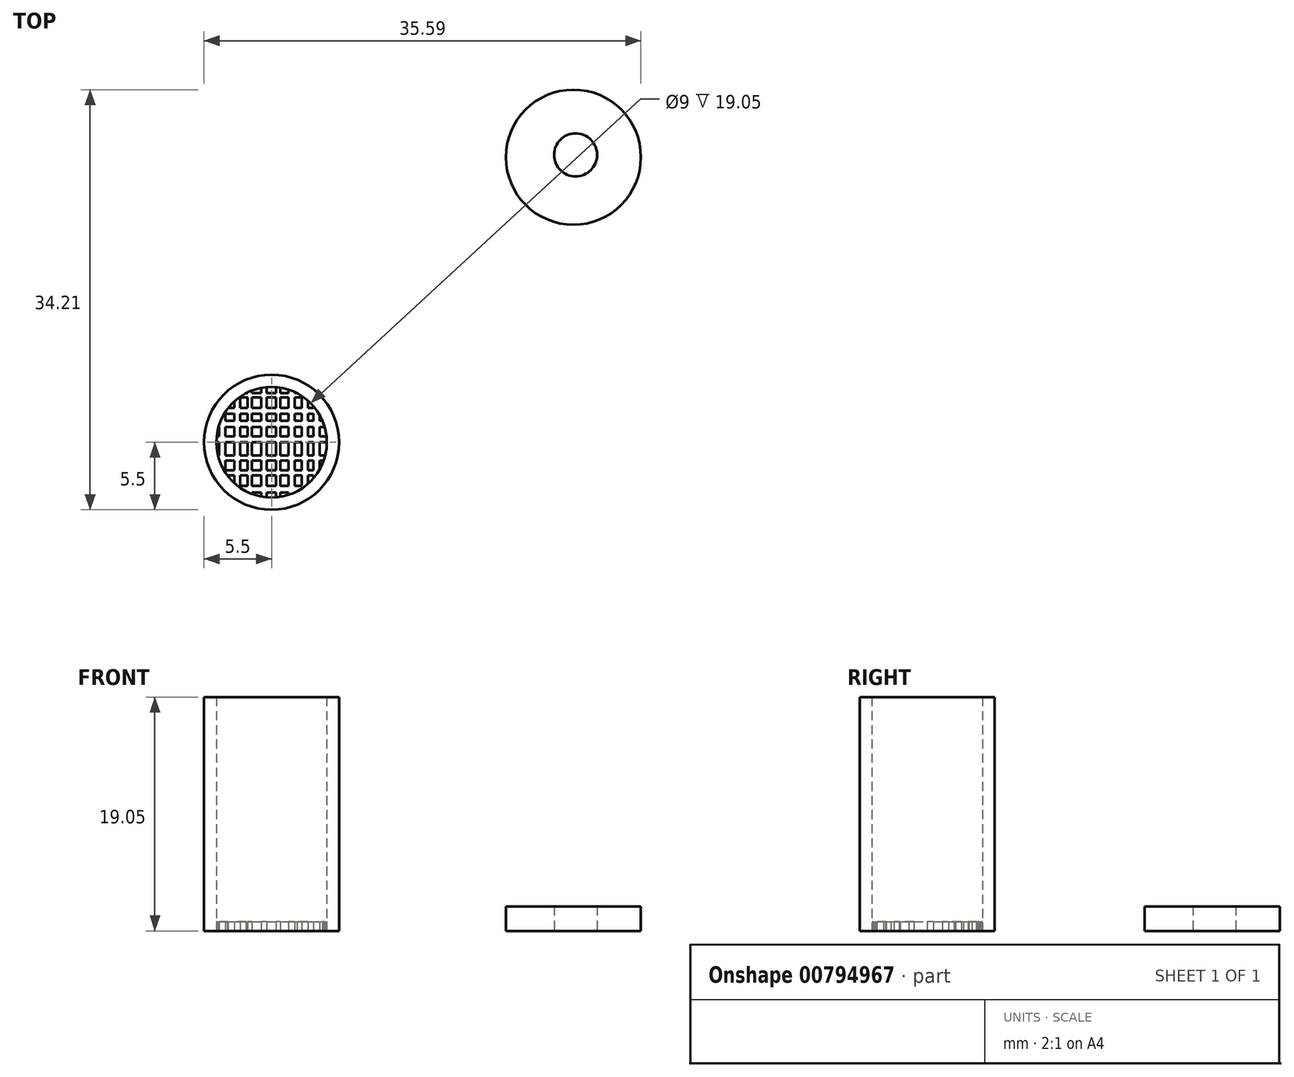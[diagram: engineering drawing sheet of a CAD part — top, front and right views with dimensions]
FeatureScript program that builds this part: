
annotation { "Feature Type Name" : "Feature", "Feature Type Description" : "" }
export const myFeature = defineFeature(function(context is Context, id is Id, definition is map)
    precondition{}
    {
        {
            var Q0;
            Q0=qCreatedBy(makeId("Top.planeOp"),FACE);
            var sketch = newSketch(context, id + "F0", { "sketchPlane" : qUnion([Q0])});
            skCircle(sketch, "E0", {"center": v(0, 0) * mm, "radius": 5.5 * mm});
            skSolve(sketch);
        }
        {
            var Q0;
            Q0=makeQuery(id+"F0.imprint","IMPRINT",FACE,{"disambiguationData":[TD([[makeQuery(id+"F0.imprint","IMPRINT",EDGE,{"derivedFrom":sQuery(id+"F0.wireOp",EDGE,"E0")}),1.0]])]});
            var Q1;
            Q1=sQuery(id+"F0.wireOp",EDGE,"E0");
            extrude(context, id + "F1", {"entities" : qUnion([Q0]), "surfaceEntities" : qUnion([Q1]), "depth" : 19.05 * mm, "offsetDistance" : 25.4 * mm});
        }
        {
            var Q0;
            Q0=qCreatedBy(makeId("Top.planeOp"),FACE);
            var sketch = newSketch(context, id + "F2", { "sketchPlane" : qUnion([Q0])});
            skCircle(sketch, "E1", {"center": v(0, 0) * mm, "radius": 4.5 * mm});
            skSolve(sketch);
        }
        {
            var Q0;
            Q0=makeQuery(id+"F2.imprint","IMPRINT",FACE,{"disambiguationData":[TD([[makeQuery(id+"F2.imprint","IMPRINT",EDGE,{"derivedFrom":sQuery(id+"F2.wireOp",EDGE,"E1")}),1.0]])]});
            extrude(context, id + "F3", {"entities" : qUnion([Q0]), "operationType" : NewBodyOperationType.REMOVE, "depth" : 76.7 * mm, "offsetDistance" : 25.4 * mm});
        }
        {
            var Q0;
            Q0=qCreatedBy(makeId("Top.planeOp"),FACE);
            var sketch = newSketch(context, id + "F4", { "sketchPlane" : qUnion([Q0])});
            skLineSegment(sketch, "E2.bottom", {"start": v(-4.27, -3.14) * mm, "end": v(-3.78, -3.14) * mm});
            skLineSegment(sketch, "E2.top", {"start": v(-4.27, 3.15) * mm, "end": v(-3.78, 3.15) * mm});
            skLineSegment(sketch, "E2.left", {"start": v(-4.27, -3.14) * mm, "end": v(-4.27, 3.15) * mm});
            skLineSegment(sketch, "E2.right", {"start": v(-3.78, -3.14) * mm, "end": v(-3.78, 3.15) * mm});
            skSolve(sketch);
        }
        {
            var Q0;
            Q0=makeQuery(id+"F4.imprint","IMPRINT",FACE,{"disambiguationData":[TD([[makeQuery(id+"F4.imprint","IMPRINT",EDGE,{"derivedFrom":sQuery(id+"F4.wireOp",EDGE,"E2.bottom")}),1.0]])]});
            extrude(context, id + "F5", {"entities" : qUnion([Q0]), "operationType" : NewBodyOperationType.ADD, "depth" : 0.76 * mm, "offsetDistance" : 25.4 * mm});
        }
        {
            var Q0;
            Q0=qCreatedBy(makeId("Top.planeOp"),FACE);
            var sketch = newSketch(context, id + "F6", { "sketchPlane" : qUnion([Q0])});
            skLineSegment(sketch, "E3.bottom", {"start": v(-3.03, -4) * mm, "end": v(-2.55, -4) * mm});
            skLineSegment(sketch, "E3.top", {"start": v(-3.03, 4.04) * mm, "end": v(-2.55, 4.04) * mm});
            skLineSegment(sketch, "E3.left", {"start": v(-3.03, -4) * mm, "end": v(-3.03, 4.04) * mm});
            skLineSegment(sketch, "E3.right", {"start": v(-2.55, -4) * mm, "end": v(-2.55, 4.04) * mm});
            skSolve(sketch);
        }
        {
            var Q0;
            Q0=makeQuery(id+"F6.imprint","IMPRINT",FACE,{"disambiguationData":[TD([[makeQuery(id+"F6.imprint","IMPRINT",EDGE,{"derivedFrom":sQuery(id+"F6.wireOp",EDGE,"E3.bottom")}),1.0]])]});
            extrude(context, id + "F7", {"entities" : qUnion([Q0]), "operationType" : NewBodyOperationType.ADD, "depth" : 0.76 * mm, "offsetDistance" : 25.4 * mm});
        }
        {
            var Q0;
            Q0=qCreatedBy(makeId("Top.planeOp"),FACE);
            var sketch = newSketch(context, id + "F8", { "sketchPlane" : qUnion([Q0])});
            skLineSegment(sketch, "E4.bottom", {"start": v(-1.96, -4.6) * mm, "end": v(-1.6, -4.6) * mm});
            skLineSegment(sketch, "E4.top", {"start": v(-1.96, 4.74) * mm, "end": v(-1.6, 4.74) * mm});
            skLineSegment(sketch, "E4.left", {"start": v(-1.96, -4.6) * mm, "end": v(-1.96, 4.74) * mm});
            skLineSegment(sketch, "E4.right", {"start": v(-1.6, -4.6) * mm, "end": v(-1.6, 4.74) * mm});
            skSolve(sketch);
        }
        {
            var Q0;
            Q0=makeQuery(id+"F8.imprint","IMPRINT",FACE,{"disambiguationData":[TD([[makeQuery(id+"F8.imprint","IMPRINT",EDGE,{"derivedFrom":sQuery(id+"F8.wireOp",EDGE,"E4.bottom")}),1.0]])]});
            extrude(context, id + "F9", {"entities" : qUnion([Q0]), "operationType" : NewBodyOperationType.ADD, "depth" : 0.76 * mm, "offsetDistance" : 25.4 * mm});
        }
        {
            var Q0;
            Q0=qCreatedBy(makeId("Top.planeOp"),FACE);
            var sketch = newSketch(context, id + "F10", { "sketchPlane" : qUnion([Q0])});
            skLineSegment(sketch, "E5.bottom", {"start": v(-0.85, -5.13) * mm, "end": v(-0.4, -5.13) * mm});
            skLineSegment(sketch, "E5.top", {"start": v(-0.85, 5) * mm, "end": v(-0.4, 5) * mm});
            skLineSegment(sketch, "E5.left", {"start": v(-0.85, -5.13) * mm, "end": v(-0.85, 5) * mm});
            skLineSegment(sketch, "E5.right", {"start": v(-0.4, -5.13) * mm, "end": v(-0.4, 5) * mm});
            skSolve(sketch);
        }
        {
            var Q0;
            Q0=makeQuery(id+"F10.imprint","IMPRINT",FACE,{"disambiguationData":[TD([[makeQuery(id+"F10.imprint","IMPRINT",EDGE,{"derivedFrom":sQuery(id+"F10.wireOp",EDGE,"E5.bottom")}),1.0]])]});
            extrude(context, id + "F11", {"entities" : qUnion([Q0]), "operationType" : NewBodyOperationType.ADD, "depth" : 0.76 * mm, "offsetDistance" : 25.4 * mm});
        }
        {
            var Q0;
            Q0=qCreatedBy(makeId("Top.planeOp"),FACE);
            var sketch = newSketch(context, id + "F12", { "sketchPlane" : qUnion([Q0])});
            skLineSegment(sketch, "E6.bottom", {"start": v(0.35, -5) * mm, "end": v(0.72, -5) * mm});
            skLineSegment(sketch, "E6.top", {"start": v(0.35, 4.95) * mm, "end": v(0.72, 4.95) * mm});
            skLineSegment(sketch, "E6.left", {"start": v(0.35, -5) * mm, "end": v(0.35, 4.95) * mm});
            skLineSegment(sketch, "E6.right", {"start": v(0.72, -5) * mm, "end": v(0.72, 4.95) * mm});
            skSolve(sketch);
        }
        {
            var Q0;
            Q0=makeQuery(id+"F12.imprint","IMPRINT",FACE,{"disambiguationData":[TD([[makeQuery(id+"F12.imprint","IMPRINT",EDGE,{"derivedFrom":sQuery(id+"F12.wireOp",EDGE,"E6.bottom")}),1.0]])]});
            extrude(context, id + "F13", {"entities" : qUnion([Q0]), "operationType" : NewBodyOperationType.ADD, "depth" : 0.76 * mm, "offsetDistance" : 25.4 * mm});
        }
        {
            var Q0;
            Q0=qCreatedBy(makeId("Top.planeOp"),FACE);
            var sketch = newSketch(context, id + "F14", { "sketchPlane" : qUnion([Q0])});
            skLineSegment(sketch, "E7.bottom", {"start": v(1.38, -4.88) * mm, "end": v(1.88, -4.88) * mm});
            skLineSegment(sketch, "E7.top", {"start": v(1.38, 4.62) * mm, "end": v(1.88, 4.62) * mm});
            skLineSegment(sketch, "E7.left", {"start": v(1.38, -4.88) * mm, "end": v(1.38, 4.62) * mm});
            skLineSegment(sketch, "E7.right", {"start": v(1.88, -4.88) * mm, "end": v(1.88, 4.62) * mm});
            skSolve(sketch);
        }
        {
            var Q0;
            Q0=makeQuery(id+"F14.imprint","IMPRINT",FACE,{"disambiguationData":[TD([[makeQuery(id+"F14.imprint","IMPRINT",EDGE,{"derivedFrom":sQuery(id+"F14.wireOp",EDGE,"E7.bottom")}),1.0]])]});
            extrude(context, id + "F15", {"entities" : qUnion([Q0]), "operationType" : NewBodyOperationType.ADD, "depth" : 0.76 * mm, "offsetDistance" : 25.4 * mm});
        }
        {
            var Q0;
            Q0=qCreatedBy(makeId("Top.planeOp"),FACE);
            var sketch = newSketch(context, id + "F16", { "sketchPlane" : qUnion([Q0])});
            skLineSegment(sketch, "E8.bottom", {"start": v(2.47, -4.47) * mm, "end": v(2.95, -4.47) * mm});
            skLineSegment(sketch, "E8.top", {"start": v(2.47, 4.18) * mm, "end": v(2.95, 4.18) * mm});
            skLineSegment(sketch, "E8.left", {"start": v(2.47, -4.47) * mm, "end": v(2.47, 4.18) * mm});
            skLineSegment(sketch, "E8.right", {"start": v(2.95, -4.47) * mm, "end": v(2.95, 4.18) * mm});
            skSolve(sketch);
        }
        {
            var Q0;
            Q0=makeQuery(id+"F16.imprint","IMPRINT",FACE,{"disambiguationData":[TD([[makeQuery(id+"F16.imprint","IMPRINT",EDGE,{"derivedFrom":sQuery(id+"F16.wireOp",EDGE,"E8.bottom")}),1.0]])]});
            extrude(context, id + "F17", {"entities" : qUnion([Q0]), "operationType" : NewBodyOperationType.ADD, "depth" : 0.76 * mm, "offsetDistance" : 25.4 * mm});
        }
        {
            var Q0;
            Q0=qCreatedBy(makeId("Top.planeOp"),FACE);
            var sketch = newSketch(context, id + "F18", { "sketchPlane" : qUnion([Q0])});
            skLineSegment(sketch, "E9.bottom", {"start": v(3.4, -3.7) * mm, "end": v(3.92, -3.7) * mm});
            skLineSegment(sketch, "E9.top", {"start": v(3.4, 3.35) * mm, "end": v(3.92, 3.35) * mm});
            skLineSegment(sketch, "E9.left", {"start": v(3.4, -3.7) * mm, "end": v(3.4, 3.35) * mm});
            skLineSegment(sketch, "E9.right", {"start": v(3.92, -3.7) * mm, "end": v(3.92, 3.35) * mm});
            skSolve(sketch);
        }
        {
            var Q0;
            Q0=makeQuery(id+"F18.imprint","IMPRINT",FACE,{"disambiguationData":[TD([[makeQuery(id+"F18.imprint","IMPRINT",EDGE,{"derivedFrom":sQuery(id+"F18.wireOp",EDGE,"E9.bottom")}),1.0]])]});
            extrude(context, id + "F19", {"entities" : qUnion([Q0]), "operationType" : NewBodyOperationType.ADD, "depth" : 0.76 * mm, "offsetDistance" : 25.4 * mm});
        }
        {
            var Q0;
            Q0=qCreatedBy(makeId("Top.planeOp"),FACE);
            var sketch = newSketch(context, id + "F20", { "sketchPlane" : qUnion([Q0])});
            skLineSegment(sketch, "E10.bottom", {"start": v(-3.42, -4.1) * mm, "end": v(3.33, -4.1) * mm});
            skLineSegment(sketch, "E10.top", {"start": v(-3.42, -3.57) * mm, "end": v(3.33, -3.57) * mm});
            skLineSegment(sketch, "E10.left", {"start": v(-3.42, -4.1) * mm, "end": v(-3.42, -3.57) * mm});
            skLineSegment(sketch, "E10.right", {"start": v(3.33, -4.1) * mm, "end": v(3.33, -3.57) * mm});
            skSolve(sketch);
        }
        {
            var Q0;
            Q0=makeQuery(id+"F20.imprint","IMPRINT",FACE,{"disambiguationData":[TD([[makeQuery(id+"F20.imprint","IMPRINT",EDGE,{"derivedFrom":sQuery(id+"F20.wireOp",EDGE,"E10.bottom")}),1.0]])]});
            extrude(context, id + "F21", {"entities" : qUnion([Q0]), "operationType" : NewBodyOperationType.ADD, "depth" : 0.76 * mm, "offsetDistance" : 25.4 * mm});
        }
        {
            var Q0;
            Q0=qCreatedBy(makeId("Top.planeOp"),FACE);
            var sketch = newSketch(context, id + "F22", { "sketchPlane" : qUnion([Q0])});
            skLineSegment(sketch, "E11.bottom", {"start": v(-4.08, -2.7) * mm, "end": v(4.2, -2.7) * mm});
            skLineSegment(sketch, "E11.top", {"start": v(-4.08, -2.3) * mm, "end": v(4.2, -2.3) * mm});
            skLineSegment(sketch, "E11.left", {"start": v(-4.08, -2.7) * mm, "end": v(-4.08, -2.3) * mm});
            skLineSegment(sketch, "E11.right", {"start": v(4.2, -2.7) * mm, "end": v(4.2, -2.3) * mm});
            skSolve(sketch);
        }
        {
            var Q0;
            Q0=makeQuery(id+"F22.imprint","IMPRINT",FACE,{"disambiguationData":[TD([[makeQuery(id+"F22.imprint","IMPRINT",EDGE,{"derivedFrom":sQuery(id+"F22.wireOp",EDGE,"E11.bottom")}),1.0]])]});
            extrude(context, id + "F23", {"entities" : qUnion([Q0]), "operationType" : NewBodyOperationType.ADD, "depth" : 0.76 * mm, "offsetDistance" : 25.4 * mm});
        }
        {
            var Q0;
            Q0=qCreatedBy(makeId("Top.planeOp"),FACE);
            var sketch = newSketch(context, id + "F24", { "sketchPlane" : qUnion([Q0])});
            skLineSegment(sketch, "E12.bottom", {"start": v(-4.87, -1.5) * mm, "end": v(5, -1.5) * mm});
            skLineSegment(sketch, "E12.top", {"start": v(-4.87, -1.07) * mm, "end": v(5, -1.07) * mm});
            skLineSegment(sketch, "E12.left", {"start": v(-4.87, -1.5) * mm, "end": v(-4.87, -1.07) * mm});
            skLineSegment(sketch, "E12.right", {"start": v(5, -1.5) * mm, "end": v(5, -1.07) * mm});
            skSolve(sketch);
        }
        {
            var Q0;
            Q0=makeQuery(id+"F24.imprint","IMPRINT",FACE,{"disambiguationData":[TD([[makeQuery(id+"F24.imprint","IMPRINT",EDGE,{"derivedFrom":sQuery(id+"F24.wireOp",EDGE,"E12.bottom")}),1.0]])]});
            extrude(context, id + "F25", {"entities" : qUnion([Q0]), "operationType" : NewBodyOperationType.ADD, "depth" : 0.76 * mm, "offsetDistance" : 25.4 * mm});
        }
        {
            var Q0;
            Q0=qCreatedBy(makeId("Top.planeOp"),FACE);
            var sketch = newSketch(context, id + "F26", { "sketchPlane" : qUnion([Q0])});
            skLineSegment(sketch, "E13.bottom", {"start": v(-4.98, 0) * mm, "end": v(4.97, 0) * mm});
            skLineSegment(sketch, "E13.top", {"start": v(-4.98, 0.49) * mm, "end": v(4.97, 0.49) * mm});
            skLineSegment(sketch, "E13.left", {"start": v(-4.98, 0) * mm, "end": v(-4.98, 0.49) * mm});
            skLineSegment(sketch, "E13.right", {"start": v(4.97, 0) * mm, "end": v(4.97, 0.49) * mm});
            skSolve(sketch);
        }
        {
            var Q0;
            Q0=makeQuery(id+"F26.imprint","IMPRINT",FACE,{"disambiguationData":[TD([[makeQuery(id+"F26.imprint","IMPRINT",EDGE,{"derivedFrom":sQuery(id+"F26.wireOp",EDGE,"E13.bottom")}),1.0]])]});
            extrude(context, id + "F27", {"entities" : qUnion([Q0]), "operationType" : NewBodyOperationType.ADD, "depth" : 0.76 * mm, "offsetDistance" : 25.4 * mm});
        }
        {
            var Q0;
            Q0=qCreatedBy(makeId("Top.planeOp"),FACE);
            var sketch = newSketch(context, id + "F28", { "sketchPlane" : qUnion([Q0])});
            skLineSegment(sketch, "E14.bottom", {"start": v(-4.72, 1.23) * mm, "end": v(4.8, 1.23) * mm});
            skLineSegment(sketch, "E14.top", {"start": v(-4.72, 1.74) * mm, "end": v(4.8, 1.74) * mm});
            skLineSegment(sketch, "E14.left", {"start": v(-4.72, 1.23) * mm, "end": v(-4.72, 1.74) * mm});
            skLineSegment(sketch, "E14.right", {"start": v(4.8, 1.23) * mm, "end": v(4.8, 1.74) * mm});
            skSolve(sketch);
        }
        {
            var Q0;
            Q0=makeQuery(id+"F28.imprint","IMPRINT",FACE,{"disambiguationData":[TD([[makeQuery(id+"F28.imprint","IMPRINT",EDGE,{"derivedFrom":sQuery(id+"F28.wireOp",EDGE,"E14.bottom")}),1.0]])]});
            extrude(context, id + "F29", {"entities" : qUnion([Q0]), "operationType" : NewBodyOperationType.ADD, "depth" : 0.76 * mm, "offsetDistance" : 25.4 * mm});
        }
        {
            var Q0;
            Q0=qCreatedBy(makeId("Top.planeOp"),FACE);
            var sketch = newSketch(context, id + "F30", { "sketchPlane" : qUnion([Q0])});
            skLineSegment(sketch, "E15.bottom", {"start": v(-4.41, 2.3) * mm, "end": v(4.45, 2.3) * mm});
            skLineSegment(sketch, "E15.top", {"start": v(-4.41, 2.78) * mm, "end": v(4.45, 2.78) * mm});
            skLineSegment(sketch, "E15.left", {"start": v(-4.41, 2.3) * mm, "end": v(-4.41, 2.78) * mm});
            skLineSegment(sketch, "E15.right", {"start": v(4.45, 2.3) * mm, "end": v(4.45, 2.78) * mm});
            skSolve(sketch);
        }
        {
            var Q0;
            Q0=makeQuery(id+"F30.imprint","IMPRINT",FACE,{"disambiguationData":[TD([[makeQuery(id+"F30.imprint","IMPRINT",EDGE,{"derivedFrom":sQuery(id+"F30.wireOp",EDGE,"E15.bottom")}),1.0]])]});
            extrude(context, id + "F31", {"entities" : qUnion([Q0]), "operationType" : NewBodyOperationType.ADD, "depth" : 0.76 * mm, "offsetDistance" : 25.4 * mm});
        }
        {
            var Q0;
            Q0=qCreatedBy(makeId("Top.planeOp"),FACE);
            var sketch = newSketch(context, id + "F32", { "sketchPlane" : qUnion([Q0])});
            skLineSegment(sketch, "E16.bottom", {"start": v(-3.16, 3.65) * mm, "end": v(3.29, 3.65) * mm});
            skLineSegment(sketch, "E16.top", {"start": v(-3.16, 4) * mm, "end": v(3.29, 4) * mm});
            skLineSegment(sketch, "E16.left", {"start": v(-3.16, 3.65) * mm, "end": v(-3.16, 4) * mm});
            skLineSegment(sketch, "E16.right", {"start": v(3.29, 3.65) * mm, "end": v(3.29, 4) * mm});
            skSolve(sketch);
        }
        {
            var Q0;
            Q0=makeQuery(id+"F32.imprint","IMPRINT",FACE,{"disambiguationData":[TD([[makeQuery(id+"F32.imprint","IMPRINT",EDGE,{"derivedFrom":sQuery(id+"F32.wireOp",EDGE,"E16.bottom")}),1.0]])]});
            extrude(context, id + "F33", {"entities" : qUnion([Q0]), "operationType" : NewBodyOperationType.ADD, "depth" : 0.76 * mm, "offsetDistance" : 25.4 * mm});
        }
        {
            var Q0;
            Q0=qCreatedBy(makeId("Top.planeOp"),FACE);
            var sketch = newSketch(context, id + "F34", { "sketchPlane" : qUnion([Q0])});
            skCircle(sketch, "E17", {"center": v(24.59, 23.21) * mm, "radius": 5.5 * mm});
            skSolve(sketch);
        }
        {
            var Q0;
            Q0 = qSketchRegion(id + "F34", true);
            extrude(context, id + "F35", {"entities" : qUnion([Q0]), "depth" : 2 * mm, "offsetDistance" : 25.4 * mm});
        }
        {
            var Q0;
            Q0=qCreatedBy(makeId("Top.planeOp"),FACE);
            var sketch = newSketch(context, id + "F36", { "sketchPlane" : qUnion([Q0])});
            skCircle(sketch, "E18", {"center": v(24.77, 23.4) * mm, "radius": 1.75 * mm});
            skSolve(sketch);
        }
        {
            var Q0;
            Q0=makeQuery(id+"F36.imprint","IMPRINT",FACE,{"disambiguationData":[TD([[makeQuery(id+"F36.imprint","IMPRINT",EDGE,{"derivedFrom":sQuery(id+"F36.wireOp",EDGE,"E18")}),1.0]])]});
            var Q1;
            Q1=sQuery(id+"F36.wireOp",EDGE,"E18");
            extrude(context, id + "F37", {"entities" : qUnion([Q0]), "operationType" : NewBodyOperationType.REMOVE, "surfaceEntities" : qUnion([Q1]), "depth" : 19.79 * mm, "offsetDistance" : 25.4 * mm});
        }
    });
